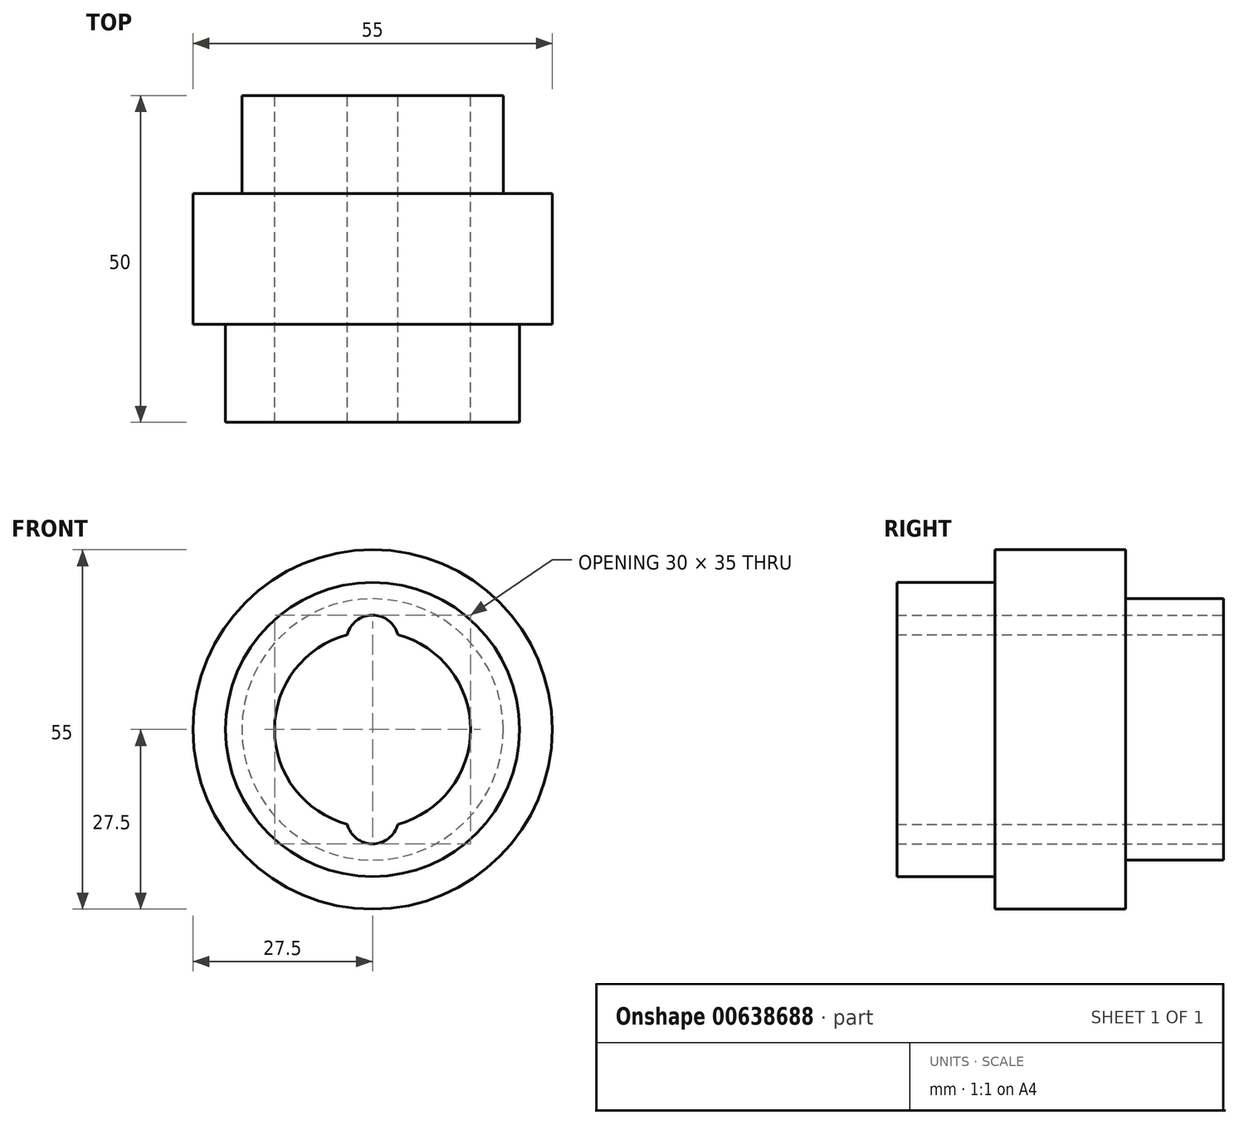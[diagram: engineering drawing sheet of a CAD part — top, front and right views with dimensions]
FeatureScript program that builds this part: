
annotation { "Feature Type Name" : "Feature", "Feature Type Description" : "" }
export const myFeature = defineFeature(function(context is Context, id is Id, definition is map)
    precondition{}
    {
        {
            var Q0;
            Q0=qCreatedBy(makeId("Front.planeOp"),FACE);
            var sketch = newSketch(context, id + "F0", { "sketchPlane" : qUnion([Q0])});
            skCircle(sketch, "E0", {"center": v(0, 0) * mm, "radius": 15 * mm});
            skCircle(sketch, "E1", {"center": v(0, 0) * mm, "radius": 20 * mm});
            skLineSegment(sketch, "E2", {"start": v(-4, 13.5) * mm, "end": v(4, 13.5) * mm});
            skArc(sketch, "E3", {"start": v(4, 13.5) * mm, "mid": v(0, 17.5) * mm, "end": v(-4, 13.5) * mm});
            skArc(sketch, "E4.MirrorCS", {"start": v(4, -13.5) * mm, "mid": v(0, -17.5) * mm, "end": v(-4, -13.5) * mm});
            skLineSegment(sketch, "E5.MirrorCS", {"start": v(-4, -13.5) * mm, "end": v(4, -13.5) * mm});
            skSolve(sketch);
        }
        {
            var Q0;
            Q0=qSketchRegion(id+"F0",true);
            extrude(context, id + "F1", {"entities" : qUnion([Q0]), "depth" : 50 * mm, "offsetDistance" : 25 * mm});
        }
        {
            var Q0;
            Q0=makeQuery(id+"F1.opExtrude","CAP_FACE",FACE,{"disambiguationData":[OSD([sQuery(id+"F0.wireOp",EDGE,"E0"),sQuery(id+"F0.wireOp",EDGE,"E1"),sQuery(id+"F0.wireOp",EDGE,"E3"),sQuery(id+"F0.wireOp",EDGE,"E4.MirrorCS")])],"isStart":false});
            var sketch = newSketch(context, id + "F2", { "sketchPlane" : qUnion([Q0])});
            skCircle(sketch, "E6", {"center": v(0, 0) * mm, "radius": 27.5 * mm});
            skCircle(sketch, "E7", {"center": v(0, 0) * mm, "radius": 20 * mm});
            skSolve(sketch);
        }
        {
            var Q0;
            Q0=qSketchRegion(id+"F2",true);
            extrude(context, id + "F3", {"entities" : qUnion([Q0]), "operationType" : NewBodyOperationType.ADD, "oppositeDirection" : true, "depth" : 35 * mm, "offsetDistance" : 25 * mm});
        }
        {
            var Q0;
            Q0=makeQuery(id+"F3.boolean.opBoolean","MERGE",FACE,{"derivedFrom":[makeQuery(id+"F1.opExtrude","CAP_FACE",FACE,{"disambiguationData":[OSD([sQuery(id+"F0.wireOp",EDGE,"E0"),sQuery(id+"F0.wireOp",EDGE,"E1"),sQuery(id+"F0.wireOp",EDGE,"E3"),sQuery(id+"F0.wireOp",EDGE,"E4.MirrorCS")])],"isStart":false}),makeQuery(id+"F3.opExtrude","CAP_FACE",FACE,{"disambiguationData":[OSD([sQuery(id+"F2.wireOp",EDGE,"E6"),sQuery(id+"F2.wireOp",EDGE,"E7")])],"isStart":true})]});
            var sketch = newSketch(context, id + "F4", { "sketchPlane" : qUnion([Q0])});
            skCircle(sketch, "E8", {"center": v(0, 0) * mm, "radius": 22.5 * mm});
            skCircle(sketch, "E9", {"center": v(0, 0) * mm, "radius": 29.75 * mm});
            skSolve(sketch);
        }
        {
            var Q0;
            Q0 = qSketchRegion(id + "F4", true);
            extrude(context, id + "F5", {"entities" : qUnion([Q0]), "operationType" : NewBodyOperationType.REMOVE, "oppositeDirection" : true, "depth" : 15 * mm, "offsetDistance" : 25 * mm});
        }
    });
